# Revit family: Gi605H
name_source: partatom
category: Equipement spécialisé
units: mm (PartAtom-declared; Revit-internal decimal feet)

## family parameters
Basée sur le plan de construction = Non
Conserver l'orientation des annotations = Non
Cote de connecteur circulaire = Utiliser le diamètre
Couper avec des vides une fois chargée = Non
Numéro OmniClass = 23.40.40.14
Partagée = Non
Repère de localisation dans la pièce = Non
Titre OmniClass = Food Service Equipment
Toujours verticalement = Oui
Type d'élément = Normal

## types (2) — shared parameters
Altezza allacciamento elettrico da pavimento finito = 135 mm  [stored 0.442913 ft]
Altezza da terra raccordo acqua calda = 175 mm  [stored 0.574147 ft]
Altezza dello scarico diretto acqua da pavimento finito = 145 mm  [stored 0.475722 ft]
Corrente di funzionamento normale = 14 A
Description = THREE-PHASE FRONT LOADING POTWASHER WITH RCD
Diametro dello scarico diretto di acqua = 1 1/2"
Diametro raccordo acqua calda = 1"
Fabricant = COMENDA
Fase = 3
Frequenza = 50 Hz
Lunghezza = 860 mm
Numero dei poli = 3
Peso netto = 200.00 kg
Pessione minima acqua fredda = 200000.0 Pa
Potenza elettrica = 9000 W
Pressione minima acqua calda = 200000.0 Pa
Protezione contro le sovracorrenti = 16 A
Temperatura raccomandata per acqua calda = 50 °C
Tensione = 400 V
URL = www.comenda.fr
URL catalogo = https://www.comenda.fr
zero-valued in all types: Elévation par défaut

## per-type parameters (varying)
| type | Altezza | Modèle | Profondità |
| 6G3256_AA | 2295 mm  [stored 7.52953 ft] | Gi 605H R CRC | 900 mm  [stored 2.95276 ft] |
| 6G3151_AA | 2145 mm  [stored 7.0374 ft] | Gi 605 R CRC | 870 mm  [stored 2.85433 ft] |

note: [stored X ft] marks values corroborated as IEEE doubles in the binary element streams (Revit-internal decimal feet)

## geometry (parser evidence)
native form markers: Sweep x3
no freeform markers — native parametric forms only
